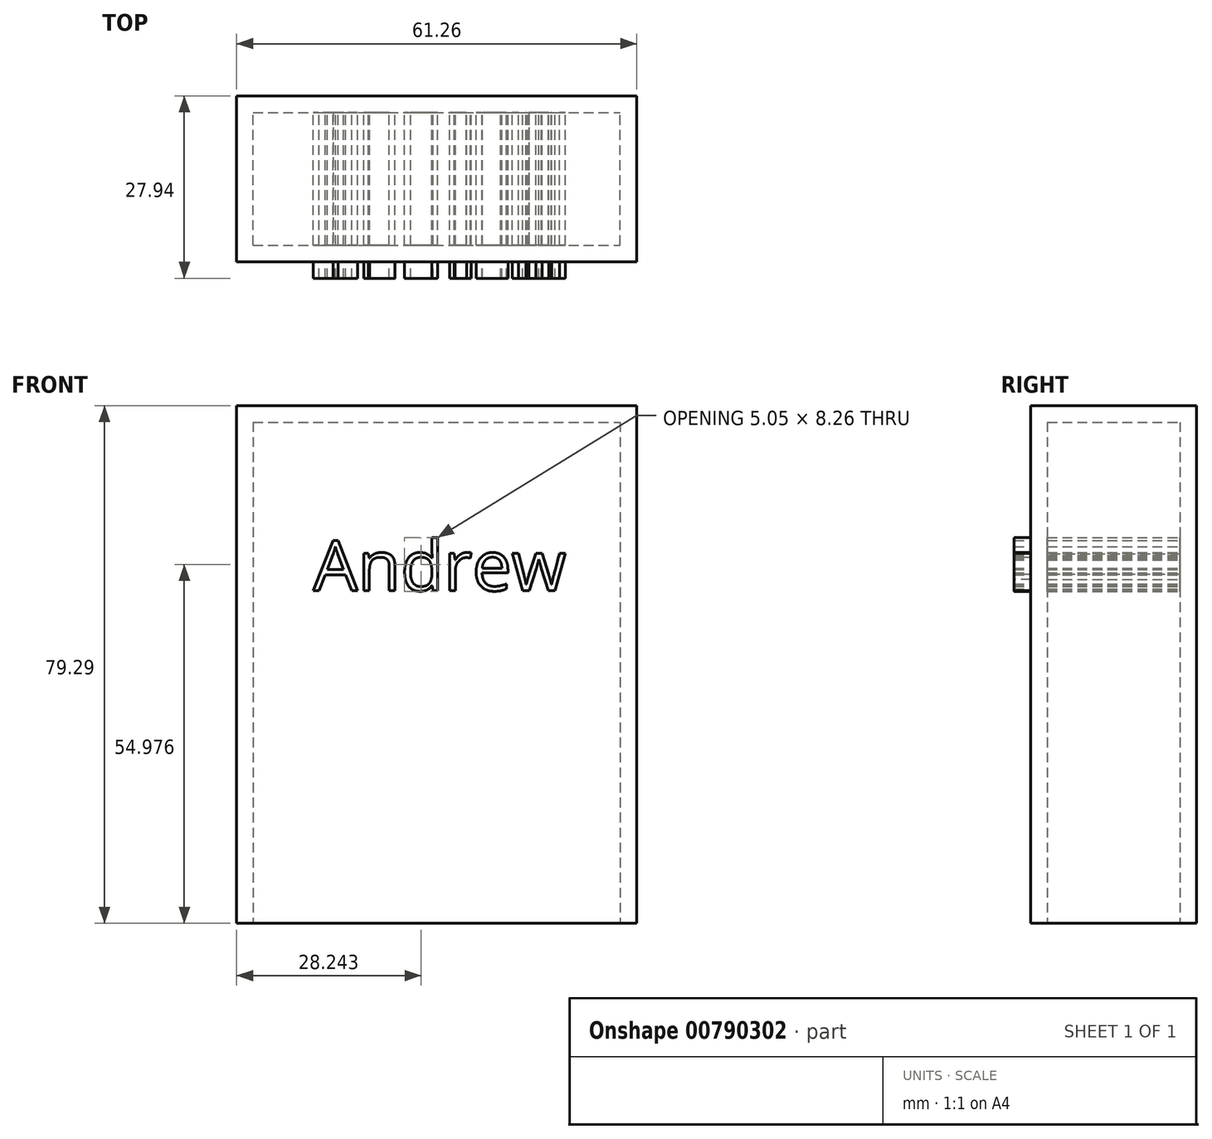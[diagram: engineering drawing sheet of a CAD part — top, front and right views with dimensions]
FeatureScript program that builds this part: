
annotation { "Feature Type Name" : "Feature", "Feature Type Description" : "" }
export const myFeature = defineFeature(function(context is Context, id is Id, definition is map)
    precondition{}
    {
        {
            var Q0;
            Q0=qCreatedBy(makeId("Front.planeOp"),FACE);
            var sketch = newSketch(context, id + "F0", { "sketchPlane" : qUnion([Q0])});
            skLineSegment(sketch, "E0.bottom", {"start": v(-32.2, 38.07) * mm, "end": v(29.06, 38.07) * mm});
            skLineSegment(sketch, "E0.top", {"start": v(-32.2, -41.22) * mm, "end": v(29.06, -41.22) * mm});
            skLineSegment(sketch, "E0.left", {"start": v(-32.2, 38.07) * mm, "end": v(-32.2, -41.22) * mm});
            skLineSegment(sketch, "E0.right", {"start": v(29.06, 38.07) * mm, "end": v(29.06, -41.22) * mm});
            skSolve(sketch);
        }
        {
            var Q0;
            Q0=makeQuery(id+"F0.imprint","IMPRINT",FACE,{"disambiguationData":[TD([[makeQuery(id+"F0.imprint","IMPRINT",EDGE,{"derivedFrom":sQuery(id+"F0.wireOp",EDGE,"E0.bottom")}),-1.0]])]});
            extrude(context, id + "F1", {"entities" : qUnion([Q0]), "depth" : 25.4 * mm, "offsetDistance" : 25.4 * mm});
        }
        {
            var Q0;
            Q0=makeQuery(id+"F1.opExtrude","SWEPT_FACE",FACE,{"disambiguationData":[OSD([sQuery(id+"F0.wireOp",EDGE,"E0.top")])]});
            shell(context, id + "F2", {"entities" : qUnion([Q0]), "thickness" : 2.54 * mm});
        }
        {
            var Q0;
            Q0=qCreatedBy(makeId("Front.planeOp"),FACE);
            var sketch = newSketch(context, id + "F3", { "sketchPlane" : qUnion([Q0])});
            skText(sketch, "E1", { "text": "Andrew\n", "fontName": "OpenSans-Regular.ttf"});
            const initialGuessF3  = {"E1": [-0.02047, 0.00973, 1, 0, 0.00773]};
            skSetInitialGuess(sketch, initialGuessF3);
            skSolve(sketch);
        }
        {
            var Q0;
            Q0 = qSketchRegion(id + "F3", true);
            extrude(context, id + "F4", {"entities" : qUnion([Q0]), "operationType" : NewBodyOperationType.ADD, "depth" : 27.94 * mm, "offsetDistance" : 25.4 * mm});
        }
    });
